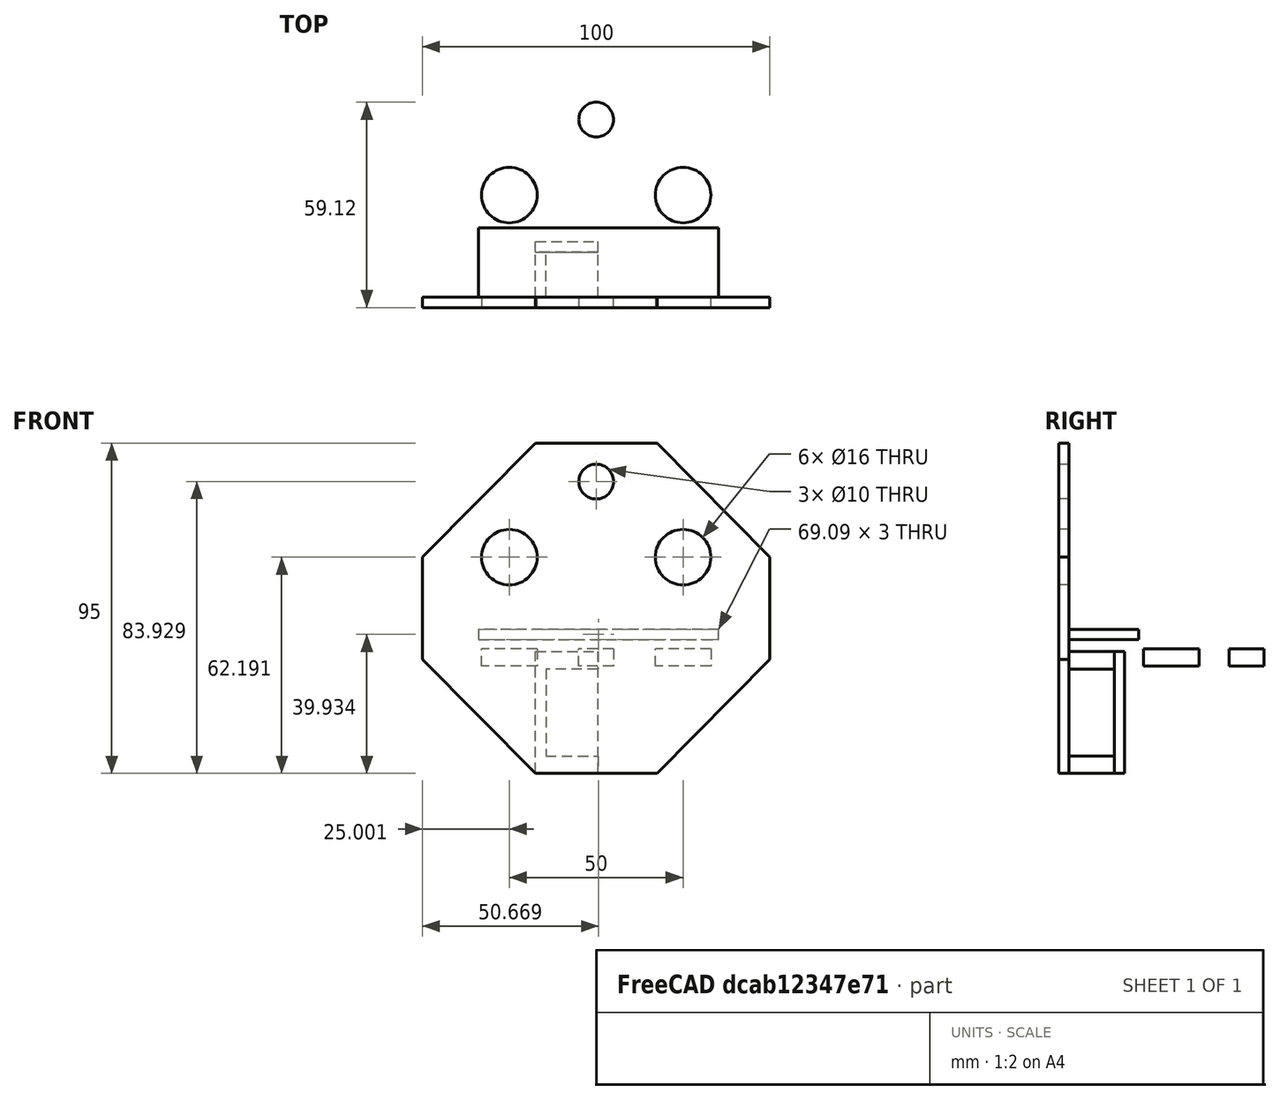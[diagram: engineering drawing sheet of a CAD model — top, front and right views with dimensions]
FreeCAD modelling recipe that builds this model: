
FCSTD DOCUMENT  (FreeCAD 0.16R6710 (Git))
Label: cabeza_v4
License: All rights reserved
LicenseURL: http://en.wikipedia.org/wiki/All_rights_reserved
objects: Sketcher::SketchObject×5, PartDesign::Pad×4, PartDesign::Pocket×1, Mesh::Feature×1
note: 15 computed .brp shape members not serialized (recipe doc carries the construction recipe); baked Part::Feature solids carry a one-line shape summary decoded from their .brp

FEATURE [Sketcher::SketchObject] Sketch
  Placement = pos=(0,0,0) rot=(-1,0,0;4.71239rad)
  sketch-geometry (8):
    g0: LineSegment StartX=-14.3786 StartY=-32.8097 StartZ=0 EndX=20.6214 EndY=-32.8097 EndZ=0
    g1: LineSegment StartX=20.6214 StartY=-32.8097 StartZ=0 EndX=53.1214 EndY=0 EndZ=0
    g2: LineSegment StartX=53.1214 StartY=0 StartZ=0 EndX=53.1214 EndY=29.3805 EndZ=0
    g3: LineSegment StartX=53.1214 StartY=29.3805 StartZ=0 EndX=20.6214 EndY=62.1903 EndZ=0
    g4: LineSegment StartX=20.6214 StartY=62.1903 StartZ=0 EndX=-14.3786 EndY=62.1903 EndZ=0
    g5: LineSegment StartX=-14.3786 StartY=62.1903 StartZ=0 EndX=-46.8786 EndY=29.3805 EndZ=0
    g6: LineSegment StartX=-46.8786 StartY=29.3805 StartZ=0 EndX=-46.8786 EndY=0 EndZ=0
    g7: LineSegment StartX=-46.8786 StartY=0 StartZ=0 EndX=-14.3786 EndY=-32.8097 EndZ=0
  constraints (22):
    c: Horizontal(g0)
    c: Coincident(g0,g1)
    c: Coincident(g1,g2)
    c: Vertical(g2)
    c: Coincident(g2,g3)
    c: Coincident(g3,g4)
    c: Horizontal(g4)
    c: Coincident(g4,g5)
    c: Coincident(g5,g6)
    c: Coincident(g6,g7)
    c: Coincident(g7,g0)
    c: Equal(g7,g5)
    c: Equal(g5,g3)
    c: Equal(g3,g1)
    c: Vertical(g6)
    c: PointOnObject(g6,g-1)
    c: PointOnObject(g1,g-1)
    c: DistanceX(g0,g0) = 35
    c: Equal(g4,g0)
    c: Equal(g6,g2)
    c: Distance(g6,g1) = 100
    c: Distance(g3,g0) = 95
FEATURE [PartDesign::Pad] Pad
  Length = 3
  Length2 = 100
  Placement = pos=(0,0,0) rot=(-1,0,0;4.71239rad)
  Sketch = -> Sketch
  Type = 0
FEATURE [Sketcher::SketchObject] Sketch001
  ExternalGeometry = -> [Pad]
  Placement = pos=(0,-3,0) rot=(1,0,0;1.5708rad)
  Support = -> Pad [Face10]
  sketch-geometry (4):
    g0: Circle CenterX=-21.8786 CenterY=29.3805 CenterZ=0 NormalX=0 NormalY=0 NormalZ=1 Radius=8
    g1: Circle CenterX=28.1214 CenterY=29.3805 CenterZ=0 NormalX=0 NormalY=0 NormalZ=1 Radius=8
    g2: LineSegment [constr] StartX=-46.8786 StartY=29.3805 StartZ=0 EndX=53.1214 EndY=29.3805 EndZ=0
    g3: Circle CenterX=3.12 CenterY=51.1193 CenterZ=0 NormalX=0 NormalY=0 NormalZ=1 Radius=5
  constraints (9):
    c: Coincident(g2,g-3)
    c: Coincident(g2,g-4)
    c: PointOnObject(g1,g2)
    c: PointOnObject(g0,g2)
    c: Distance(g0,g1) = 50
    c: Distance(g0,g2) = 25
    c: Equal(g1,g0)
    c: Radius(g1) = 8
    c: Radius(g3) = 5
FEATURE [PartDesign::Pocket] Pocket
  Length = 5
  Placement = pos=(0,0,0) rot=(-1,0,0;4.71239rad)
  Sketch = -> Sketch001
  Type = 0
FEATURE [Mesh::Feature] _g_servo  label="9g_servo"
  Placement = pos=(0,6,-15) rot=(0,1,0;1.5708rad)
FEATURE [Sketcher::SketchObject] Sketch002
  Placement = pos=(0,0,0) rot=(-1,0,0;1.5708rad)
  Support = -> Pocket [Face4]
  sketch-geometry (4):
    g0: LineSegment StartX=-30.7543 StartY=-5.62429 StartZ=0 EndX=38.3315 EndY=-5.62429 EndZ=0
    g1: LineSegment StartX=38.3315 StartY=-5.62429 StartZ=0 EndX=38.3315 EndY=-8.62429 EndZ=0
    g2: LineSegment StartX=38.3315 StartY=-8.62429 StartZ=0 EndX=-30.7543 EndY=-8.62429 EndZ=0
    g3: LineSegment StartX=-30.7543 StartY=-8.62429 StartZ=0 EndX=-30.7543 EndY=-5.62429 EndZ=0
  constraints (9):
    c: Coincident(g0,g1)
    c: Coincident(g1,g2)
    c: Coincident(g2,g3)
    c: Coincident(g3,g0)
    c: Horizontal(g0)
    c: Horizontal(g2)
    c: Vertical(g1)
    c: Vertical(g3)
    c: DistanceY(g1,g1) = 3
FEATURE [PartDesign::Pad] Pad001
  Length = 20
  Length2 = 100
  Placement = pos=(0,0,0) rot=(-1,0,0;4.71239rad)
  Sketch = -> Sketch002
  Type = 0
FEATURE [Sketcher::SketchObject] Sketch003
  ExternalGeometry = -> [Pad001]
  Placement = pos=(0,0,0) rot=(-1,0,0;1.5708rad)
  Support = -> Pad001 [Face4]
  sketch-geometry (8):
    g0: LineSegment StartX=3.62144 StartY=2.80974 StartZ=0 EndX=-11.3786 EndY=2.80974 EndZ=0
    g1: LineSegment StartX=-11.3786 StartY=2.80974 StartZ=0 EndX=-11.3786 EndY=27.8097 EndZ=0
    g2: LineSegment StartX=-11.3786 StartY=27.8097 StartZ=0 EndX=3.60727 EndY=27.8097 EndZ=0
    g3: LineSegment StartX=3.60727 StartY=27.8097 StartZ=0 EndX=3.60727 EndY=32.8097 EndZ=0
    g4: LineSegment StartX=3.60727 StartY=32.8097 StartZ=0 EndX=-14.3786 EndY=32.8097 EndZ=0
    g5: LineSegment StartX=-14.3786 StartY=32.8097 StartZ=0 EndX=-14.3786 EndY=-2.19026 EndZ=0
    g6: LineSegment StartX=-14.3786 StartY=-2.19026 StartZ=0 EndX=3.62144 EndY=-2.19026 EndZ=0
    g7: LineSegment StartX=3.62144 StartY=-2.19026 StartZ=0 EndX=3.62144 EndY=2.80974 EndZ=0
  constraints (22):
    c: Horizontal(g0)
    c: Coincident(g0,g1)
    c: Vertical(g1)
    c: Coincident(g1,g2)
    c: Horizontal(g2)
    c: Coincident(g2,g3)
    c: Vertical(g3)
    c: Coincident(g3,g4)
    c: Horizontal(g4)
    c: Coincident(g4,g5)
    c: Vertical(g5)
    c: Coincident(g5,g6)
    c: Horizontal(g6)
    c: Coincident(g6,g7)
    c: Coincident(g7,g0)
    c: Vertical(g7)
    c: Equal(g7,g3)
    c: Distance(g0,g2) = 25
    c: DistanceY(g3,g3) = 5
    c: DistanceX(g6,g6) = 18
    c: Distance(g1,g5) = 3
    c: Coincident(g4,g-3)
FEATURE [PartDesign::Pad] Pad002
  Length = 13
  Length2 = 100
  Placement = pos=(0,0,0) rot=(-1,0,0;4.71239rad)
  Sketch = -> Sketch003
  Type = 0
FEATURE [Sketcher::SketchObject] Sketch004
  ExternalGeometry = -> [Pad002]
  Placement = pos=(0,13,0) rot=(-1,0,0;1.5708rad)
  Support = -> Pad002 [Face16]
  sketch-geometry (4):
    g0: LineSegment StartX=-14.3786 StartY=32.8097 StartZ=0 EndX=3.62144 EndY=32.8097 EndZ=0
    g1: LineSegment StartX=3.62144 StartY=32.8097 StartZ=0 EndX=3.62144 EndY=-2.19026 EndZ=0
    g2: LineSegment StartX=3.62144 StartY=-2.19026 StartZ=0 EndX=-14.3786 EndY=-2.19026 EndZ=0
    g3: LineSegment StartX=-14.3786 StartY=-2.19026 StartZ=0 EndX=-14.3786 EndY=32.8097 EndZ=0
  constraints (10):
    c: Coincident(g0,g1)
    c: Coincident(g1,g2)
    c: Coincident(g2,g3)
    c: Coincident(g3,g0)
    c: Horizontal(g0)
    c: Horizontal(g2)
    c: Vertical(g1)
    c: Vertical(g3)
    c: Coincident(g0,g-4)
    c: Coincident(g1,g-3)
FEATURE [PartDesign::Pad] Pad003
  Length = 3
  Length2 = 100
  Placement = pos=(0,0,0) rot=(-1,0,0;4.71239rad)
  Sketch = -> Sketch004
  Type = 0
